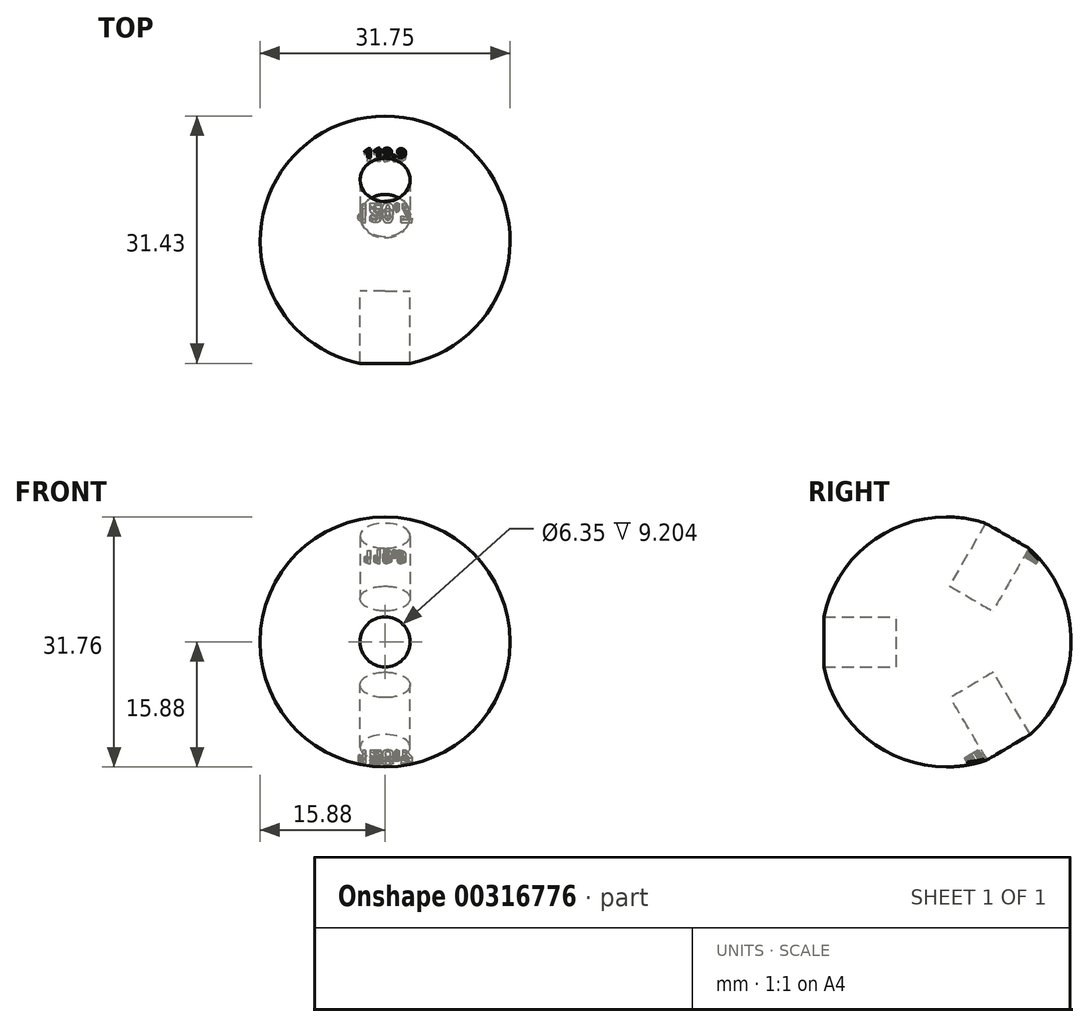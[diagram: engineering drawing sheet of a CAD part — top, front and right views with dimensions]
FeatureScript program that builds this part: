
annotation { "Feature Type Name" : "Feature", "Feature Type Description" : "" }
export const myFeature = defineFeature(function(context is Context, id is Id, definition is map)
    precondition{}
    {
        {
            var Q0;
            Q0=qCreatedBy(makeId("Front.planeOp"),FACE);
            var sketch = newSketch(context, id + "F0", { "sketchPlane" : qUnion([Q0])});
            skArc(sketch, "E0", {"start": v(0, 15.88) * mm, "mid": v(-15.88, 0) * mm, "end": v(0, -15.88) * mm});
            skLineSegment(sketch, "E1", {"start": v(0, 15.88) * mm, "end": v(0, -15.88) * mm});
            skSolve(sketch);
        }
        {
            var Q0;
            Q0=qCreatedBy(makeId("Top.planeOp"),FACE);
            var sketch = newSketch(context, id + "F1", { "sketchPlane" : qUnion([Q0])});
            skCircle(sketch, "E2", {"center": v(0, 0) * mm, "radius": 15.88 * mm});
            skSolve(sketch);
        }
        {
            var Q0;
            Q0=makeQuery(id+"F0.imprint","IMPRINT",FACE,{"disambiguationData":[TD([[makeQuery(id+"F0.imprint","IMPRINT",EDGE,{"derivedFrom":sQuery(id+"F0.wireOp",EDGE,"E0")}),1.0]])]});
            var Q1;
            Q1=sQuery(id+"F1.wireOp",EDGE,"E2");
            revolve(context, id + "F2", {"entities" : qUnion([Q0]), "axis" : qUnion([Q1]), "revolveType" : RevolveType.FULL});
        }
        {
            var Q0;
            Q0=qCreatedBy(makeId("Front.planeOp"),FACE);
            cPlane(context, id + "F3", {"entities" : qUnion([Q0]), "cplaneType" : CPlaneType.OFFSET, "offset" : 6.35 * mm, "width" : 152.4 * mm, "height" : 152.4 * mm});
        }
        {
            var Q0;
            Q0=qCreatedBy(id+"F3.planeOp",FACE);
            var sketch = newSketch(context, id + "F4", { "sketchPlane" : qUnion([Q0])});
            skCircle(sketch, "E3", {"center": v(0, 0) * mm, "radius": 3.18 * mm});
            skSolve(sketch);
        }
        {
            var Q0;
            Q0 = qSketchRegion(id + "F4", true);
            extrude(context, id + "F5", {"entities" : qUnion([Q0]), "depth" : 25.4 * mm});
        }
        {
            var Q0;
            Q0=qCreatedBy(makeId("Top.planeOp"),FACE);
            var sketch = newSketch(context, id + "F6", { "sketchPlane" : qUnion([Q0])});
            skLineSegment(sketch, "E4", {"start": v(69.95, 0) * mm, "end": v(-61.3, 0) * mm, "construction": true});
            skSolve(sketch);
        }
        {
            var Q0;
            Q0=makeQuery(id+"F5.opExtrude","SWEPT_BODY",BODY,{"disambiguationData":[OSD([sQuery(id+"F4.wireOp",EDGE,"E3")])]});
            var Q1;
            Q1=sQuery(id+"F6.wireOp",EDGE,"E4");
            transform(context, id + "F7", {"entities" : qUnion([Q0]), "transformType" : TransformType.ROTATION, "transformAxis" : qUnion([Q1]), "angle" : 119.9 * degree, "makeCopy" : true});
        }
        {
            var Q0;
            Q0=makeQuery(id+"F5.opExtrude","SWEPT_BODY",BODY,{"disambiguationData":[OSD([sQuery(id+"F4.wireOp",EDGE,"E3")])]});
            var Q1;
            Q1=sQuery(id+"F6.wireOp",EDGE,"E4");
            transform(context, id + "F8", {"entities" : qUnion([Q0]), "transformType" : TransformType.ROTATION, "transformAxis" : qUnion([Q1]), "angle" : 120.7 * degree, "oppositeDirection" : true, "makeCopy" : true});
        }
        {
            var Q0;
            Q0=makeQuery(id+"F7.opPattern","COPY",FACE,{"derivedFrom":makeQuery(id+"F5.opExtrude","CAP_FACE",FACE,{"disambiguationData":[OSD([sQuery(id+"F4.wireOp",EDGE,"E3")])],"isStart":false}),"instanceName":"1"});
            cPlane(context, id + "F9", {"entities" : qUnion([Q0]), "cplaneType" : CPlaneType.OFFSET, "offset" : 14.96 * mm, "oppositeDirection" : true, "width" : 152.4 * mm, "height" : 152.4 * mm});
        }
        {
            var Q0;
            Q0=qCreatedBy(id+"F9.planeOp",FACE);
            var sketch = newSketch(context, id + "F10", { "sketchPlane" : qUnion([Q0])});
            skText(sketch, "E5", { "text": "119.9\n", "fontName": "OpenSans-Bold.ttf"});
            const initialGuessF10  = {"E5": [-0.00276, 0.0034, 1, 0, 0.00153]};
            skSetInitialGuess(sketch, initialGuessF10);
            skSolve(sketch);
        }
        {
            var Q0;
            Q0 = qSketchRegion(id + "F10", true);
            extrude(context, id + "F11", {"entities" : qUnion([Q0]), "operationType" : NewBodyOperationType.REMOVE, "oppositeDirection" : true, "depth" : 2.44 * mm});
        }
        {
            var Q0;
            Q0=makeQuery(id+"F8.opPattern","COPY",FACE,{"derivedFrom":makeQuery(id+"F5.opExtrude","CAP_FACE",FACE,{"disambiguationData":[OSD([sQuery(id+"F4.wireOp",EDGE,"E3")])],"isStart":false}),"instanceName":"1"});
            cPlane(context, id + "F12", {"entities" : qUnion([Q0]), "cplaneType" : CPlaneType.OFFSET, "offset" : 14.88 * mm, "oppositeDirection" : true, "width" : 152.4 * mm, "height" : 152.4 * mm});
        }
        {
            var Q0;
            Q0=qCreatedBy(id+"F12.planeOp",FACE);
            var sketch = newSketch(context, id + "F13", { "sketchPlane" : qUnion([Q0])});
            skText(sketch, "E6", { "text": "120.7", "fontName": "OpenSans-Bold.ttf"});
            const initialGuessF13  = {"E6": [-0.0036, 0.00354, 1, 0, 0.00199]};
            skSetInitialGuess(sketch, initialGuessF13);
            skSolve(sketch);
        }
        {
            var Q0;
            Q0 = qSketchRegion(id + "F13", true);
            extrude(context, id + "F14", {"entities" : qUnion([Q0]), "operationType" : NewBodyOperationType.REMOVE, "oppositeDirection" : true, "depth" : 2.97 * mm});
        }
        {
            var Q0;
            Q0=makeQuery(id+"F7.opPattern","COPY",BODY,{"derivedFrom":makeQuery(id+"F5.opExtrude","SWEPT_BODY",BODY,{"disambiguationData":[OSD([sQuery(id+"F4.wireOp",EDGE,"E3")])]}),"instanceName":"1"});
            var Q1;
            Q1=makeQuery(id+"F2.opRevolve","SWEPT_BODY",BODY,{"disambiguationData":[OSD([sQuery(id+"F0.wireOp",EDGE,"E0"),sQuery(id+"F0.wireOp",EDGE,"E1")])]});
            booleanBodies(context, id + "F15", {"operationType" : BooleanOperationType.SUBTRACTION, "tools" : qUnion([Q0]), "targets" : qUnion([Q1])});
        }
        {
            var Q0;
            Q0=makeQuery(id+"F8.opPattern","COPY",BODY,{"derivedFrom":makeQuery(id+"F5.opExtrude","SWEPT_BODY",BODY,{"disambiguationData":[OSD([sQuery(id+"F4.wireOp",EDGE,"E3")])]}),"instanceName":"1"});
            var Q1;
            Q1=makeQuery(id+"F2.opRevolve","SWEPT_BODY",BODY,{"disambiguationData":[OSD([sQuery(id+"F0.wireOp",EDGE,"E0"),sQuery(id+"F0.wireOp",EDGE,"E1")])]});
            booleanBodies(context, id + "F16", {"operationType" : BooleanOperationType.SUBTRACTION, "tools" : qUnion([Q0]), "targets" : qUnion([Q1])});
        }
        {
            var Q0;
            Q0=makeQuery(id+"F5.opExtrude","SWEPT_BODY",BODY,{"disambiguationData":[OSD([sQuery(id+"F4.wireOp",EDGE,"E3")])]});
            var Q1;
            Q1=makeQuery(id+"F2.opRevolve","SWEPT_BODY",BODY,{"disambiguationData":[OSD([sQuery(id+"F0.wireOp",EDGE,"E0"),sQuery(id+"F0.wireOp",EDGE,"E1")])]});
            booleanBodies(context, id + "F17", {"operationType" : BooleanOperationType.SUBTRACTION, "tools" : qUnion([Q0]), "targets" : qUnion([Q1])});
        }
    });
